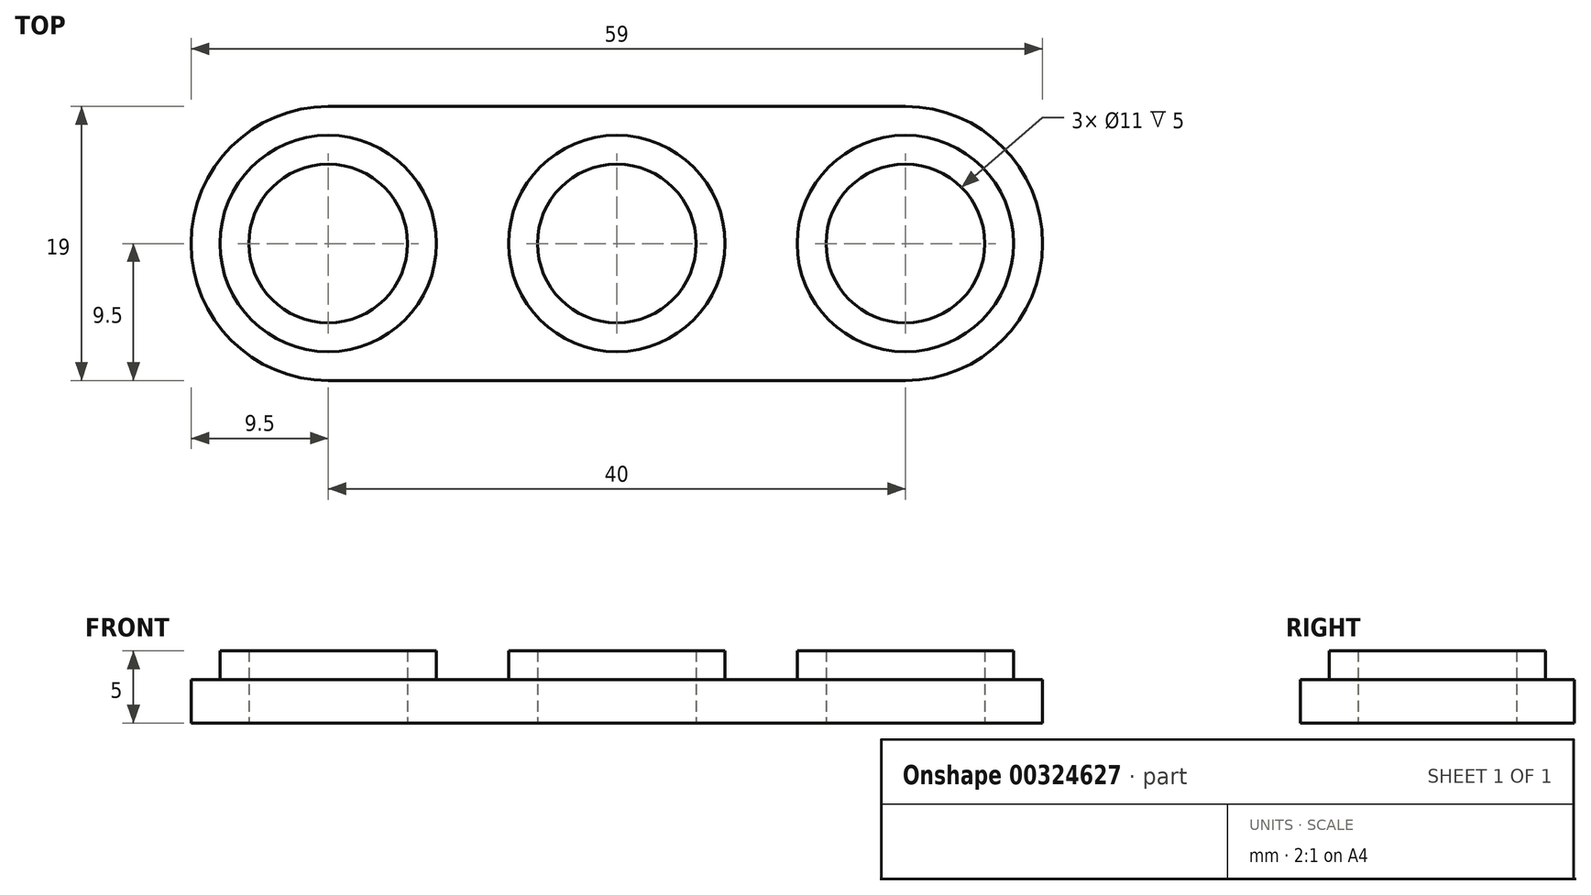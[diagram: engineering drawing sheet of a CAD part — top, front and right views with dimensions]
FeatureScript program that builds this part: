
annotation { "Feature Type Name" : "Feature", "Feature Type Description" : "" }
export const myFeature = defineFeature(function(context is Context, id is Id, definition is map)
    precondition{}
    {
        {
            assignVariable(context, id + "F0", {"name" : "e", "anyValue" : 3});
        }
        {
            assignVariable(context, id + "F1", {"name" : "h0", "anyValue" : 2});
        }
        {
            var Q0;
            Q0=qCreatedBy(makeId("Top.planeOp"),FACE);
            var sketch = newSketch(context, id + "F2", { "sketchPlane" : qUnion([Q0])});
            skLineSegment(sketch, "E0.bottom", {"start": v(0, 9.5) * mm, "end": v(40, 9.5) * mm});
            skLineSegment(sketch, "E0.top", {"start": v(0, -9.5) * mm, "end": v(40, -9.5) * mm});
            skLineSegment(sketch, "E0.left", {"start": v(-9.5, 0) * mm, "end": v(-9.5, 0) * mm});
            skLineSegment(sketch, "E0.right", {"start": v(49.5, 0) * mm, "end": v(49.5, 0) * mm});
            skPoint(sketch, "E1", {"position": v(-9.5, 0) * mm});
            skCircle(sketch, "E2", {"center": v(0, 0) * mm, "radius": 5.5 * mm});
            skPoint(sketch, "E3.visualSharp", {"position": v(49.5, 9.5) * mm});
            skArc(sketch, "E3.filletArc", {"start": v(49.5, 0) * mm, "mid": v(46.72, 6.72) * mm, "end": v(40, 9.5) * mm});
            skPoint(sketch, "E4.visualSharp", {"position": v(49.5, -9.5) * mm});
            skArc(sketch, "E4.filletArc", {"start": v(40, -9.5) * mm, "mid": v(46.72, -6.72) * mm, "end": v(49.5, 0) * mm});
            skPoint(sketch, "E5.visualSharp", {"position": v(-9.5, -9.5) * mm});
            skArc(sketch, "E5.filletArc", {"start": v(-9.5, 0) * mm, "mid": v(-6.72, -6.72) * mm, "end": v(0, -9.5) * mm});
            skPoint(sketch, "E6.visualSharp", {"position": v(-9.5, 9.5) * mm});
            skArc(sketch, "E6.filletArc", {"start": v(0, 9.5) * mm, "mid": v(-6.72, 6.72) * mm, "end": v(-9.5, 0) * mm});
            skCircle(sketch, "E7", {"center": v(0, 0) * mm, "radius": 7.5 * mm});
            skCircle(sketch, "E8.1.0.0", {"center": v(20, 0) * mm, "radius": 7.5 * mm});
            skCircle(sketch, "E8.1.0.1", {"center": v(20, 0) * mm, "radius": 5.5 * mm});
            skCircle(sketch, "E8.2.0.0", {"center": v(40, 0) * mm, "radius": 7.5 * mm});
            skCircle(sketch, "E8.2.0.1", {"center": v(40, 0) * mm, "radius": 5.5 * mm});
            skLineSegment(sketch, "E8.direction1", {"start": v(0, 0) * mm, "end": v(20, 0) * mm, "construction": true});
            skSolve(sketch);
        }
        {
            var Q0;
            Q0=qSketchRegion(id+"F2",true);
            var Q1;
            Q1=makeQuery(id+"F2.imprint","IMPRINT",FACE,{"disambiguationData":[TD([[makeQuery(id+"F2.imprint","IMPRINT",EDGE,{"derivedFrom":sQuery(id+"F2.wireOp",EDGE,"E2")}),-1.0]])]});
            var Q2;
            Q2=makeQuery(id+"F2.imprint","IMPRINT",FACE,{"disambiguationData":[TD([[makeQuery(id+"F2.imprint","IMPRINT",EDGE,{"derivedFrom":sQuery(id+"F2.wireOp",EDGE,"3f6ac68d-3e17-4b1c-9d95-bb262f7506dc.1.0.0")}),-1.0]])]});
            var Q3;
            Q3=makeQuery(id+"F2.imprint","IMPRINT",FACE,{"disambiguationData":[TD([[makeQuery(id+"F2.imprint","IMPRINT",EDGE,{"derivedFrom":sQuery(id+"F2.wireOp",EDGE,"3f6ac68d-3e17-4b1c-9d95-bb262f7506dc.2.0.0")}),-1.0]])]});
            var Q4;
            Q4=makeQuery(id+"F2.imprint","IMPRINT",FACE,{"disambiguationData":[TD([[makeQuery(id+"F2.imprint","IMPRINT",EDGE,{"derivedFrom":sQuery(id+"F2.wireOp",EDGE,"345b2114-0edb-480d-a68f-e22b198684d9.0.3.0")}),-1.0]])]});
            extrude(context, id + "F3", {"entities" : qUnion([Q0, Q1, Q2, Q3, Q4]), "depth" : (getVariable(context, 'e')) * mm});
        }
        {
            var Q0;
            Q0=makeQuery(id+"F2.imprint","IMPRINT",FACE,{"disambiguationData":[TD([[makeQuery(id+"F2.imprint","IMPRINT",EDGE,{"derivedFrom":sQuery(id+"F2.wireOp",EDGE,"E2")}),-1.0]])]});
            var Q1;
            Q1=makeQuery(id+"F2.imprint","IMPRINT",FACE,{"disambiguationData":[TD([[makeQuery(id+"F2.imprint","IMPRINT",EDGE,{"derivedFrom":sQuery(id+"F2.wireOp",EDGE,"3f6ac68d-3e17-4b1c-9d95-bb262f7506dc.1.0.0")}),-1.0]])]});
            var Q2;
            Q2=makeQuery(id+"F2.imprint","IMPRINT",FACE,{"disambiguationData":[TD([[makeQuery(id+"F2.imprint","IMPRINT",EDGE,{"derivedFrom":sQuery(id+"F2.wireOp",EDGE,"3f6ac68d-3e17-4b1c-9d95-bb262f7506dc.2.0.0")}),-1.0]])]});
            var Q3;
            Q3=makeQuery(id+"F2.imprint","IMPRINT",FACE,{"disambiguationData":[TD([[makeQuery(id+"F2.imprint","IMPRINT",EDGE,{"derivedFrom":sQuery(id+"F2.wireOp",EDGE,"345b2114-0edb-480d-a68f-e22b198684d9.0.3.0")}),-1.0]])]});
            var Q4;
            Q4=makeQuery(id+"F2.imprint","IMPRINT",FACE,{"disambiguationData":[TD([[makeQuery(id+"F2.imprint","IMPRINT",EDGE,{"derivedFrom":sQuery(id+"F2.wireOp",EDGE,"E8.1.0.0")}),1.0]])]});
            var Q5;
            Q5=makeQuery(id+"F2.imprint","IMPRINT",FACE,{"disambiguationData":[TD([[makeQuery(id+"F2.imprint","IMPRINT",EDGE,{"derivedFrom":sQuery(id+"F2.wireOp",EDGE,"E8.2.0.0")}),1.0]])]});
            extrude(context, id + "F4", {"entities" : qUnion([Q0, Q1, Q2, Q3, Q4, Q5]), "operationType" : NewBodyOperationType.ADD, "depth" : (getVariable(context, 'e') + getVariable(context, 'h0')) * mm});
        }
    });
